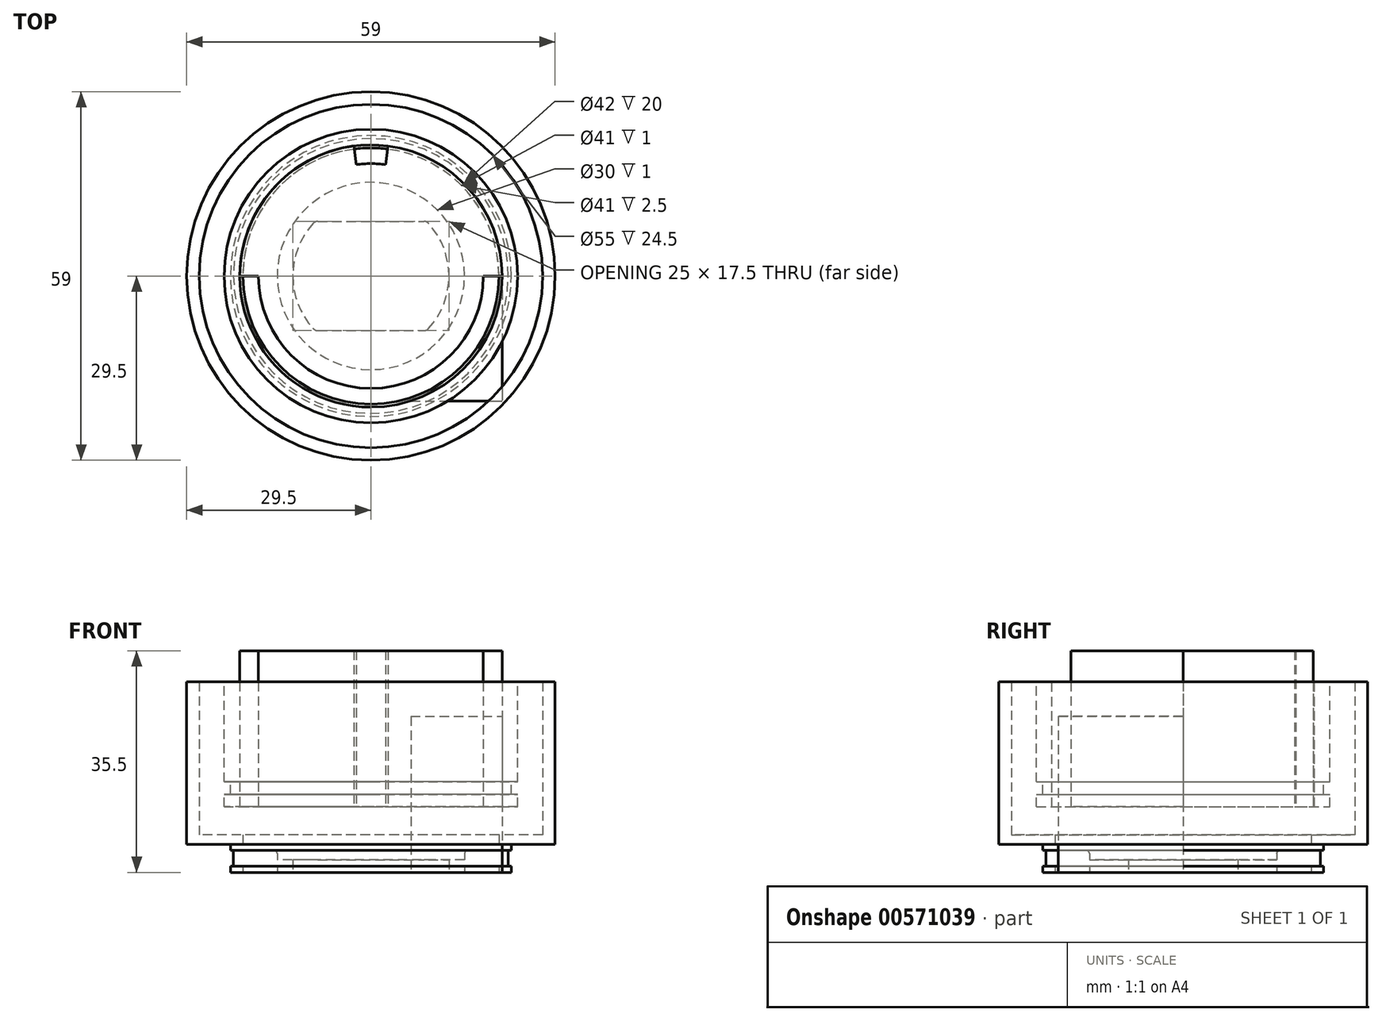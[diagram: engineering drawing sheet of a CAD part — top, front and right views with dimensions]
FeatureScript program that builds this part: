
annotation { "Feature Type Name" : "Feature", "Feature Type Description" : "" }
export const myFeature = defineFeature(function(context is Context, id is Id, definition is map)
    precondition{}
    {
        {
            var Q0;
            Q0=qCreatedBy(makeId("Top.planeOp"),FACE);
            var sketch = newSketch(context, id + "F0", { "sketchPlane" : qUnion([Q0])});
            skCircle(sketch, "E0", {"center": v(0, 0) * mm, "radius": 29.5 * mm});
            skCircle(sketch, "E1", {"center": v(0, 0) * mm, "radius": 22.5 * mm});
            skCircle(sketch, "E2", {"center": v(0, 0) * mm, "radius": 20.5 * mm});
            skCircle(sketch, "E3", {"center": v(0, 0) * mm, "radius": 15 * mm});
            skCircle(sketch, "E4", {"center": v(0, 0) * mm, "radius": 12.5 * mm, "construction": true});
            skLineSegment(sketch, "E5", {"start": v(-42, 8.75) * mm, "end": v(-42, -8.75) * mm, "construction": true});
            skPoint(sketch, "E6", {"position": v(-42, 0) * mm});
            skLineSegment(sketch, "E7", {"start": v(-8.5, 8.75) * mm, "end": v(8.5, 8.75) * mm});
            skLineSegment(sketch, "E8", {"start": v(-8.5, -8.75) * mm, "end": v(8.5, -8.75) * mm});
            skArc(sketch, "E9", {"start": v(-9.24, 8.42) * mm, "mid": v(-12.5, 0) * mm, "end": v(-9.24, -8.42) * mm});
            skArc(sketch, "E10", {"start": v(9.24, 8.42) * mm, "mid": v(12.5, 0) * mm, "end": v(9.24, -8.42) * mm});
            skPoint(sketch, "E11.visualSharp", {"position": v(-8.93, 8.75) * mm});
            skArc(sketch, "E11.filletArc", {"start": v(-8.5, 8.75) * mm, "mid": v(-8.9, 8.66) * mm, "end": v(-9.24, 8.42) * mm});
            skPoint(sketch, "E12.visualSharp", {"position": v(8.93, 8.75) * mm});
            skArc(sketch, "E12.filletArc", {"start": v(9.24, 8.42) * mm, "mid": v(8.9, 8.66) * mm, "end": v(8.5, 8.75) * mm});
            skPoint(sketch, "E13.visualSharp", {"position": v(-8.93, -8.75) * mm});
            skArc(sketch, "E13.filletArc", {"start": v(-9.24, -8.42) * mm, "mid": v(-8.9, -8.66) * mm, "end": v(-8.5, -8.75) * mm});
            skPoint(sketch, "E14.visualSharp", {"position": v(8.93, -8.75) * mm});
            skArc(sketch, "E14.filletArc", {"start": v(8.5, -8.75) * mm, "mid": v(8.9, -8.66) * mm, "end": v(9.24, -8.42) * mm});
            skCircle(sketch, "E15", {"center": v(0, 0) * mm, "radius": 22 * mm});
            skCircle(sketch, "E16", {"center": v(0, 0) * mm, "radius": 27.5 * mm});
            skSolve(sketch);
        }
        {
            var Q0;
            Q0=makeQuery(id+"F0.imprint","IMPRINT",FACE,{"disambiguationData":[TD([[makeQuery(id+"F0.imprint","IMPRINT",EDGE,{"derivedFrom":sQuery(id+"F0.wireOp",EDGE,"E1")}),1.0]])]});
            var Q1;
            Q1=makeQuery(id+"F0.imprint","IMPRINT",FACE,{"disambiguationData":[TD([[makeQuery(id+"F0.imprint","IMPRINT",EDGE,{"derivedFrom":sQuery(id+"F0.wireOp",EDGE,"E2")}),-1.0]])]});
            extrude(context, id + "F1", {"entities" : qUnion([Q0, Q1]), "depth" : 1 * mm, "offsetDistance" : 25 * mm});
        }
        {
            var Q0;
            Q0=makeQuery(id+"F0.imprint","IMPRINT",FACE,{"disambiguationData":[TD([[makeQuery(id+"F0.imprint","IMPRINT",EDGE,{"derivedFrom":sQuery(id+"F0.wireOp",EDGE,"E2")}),-1.0]])]});
            var Q1;
            Q1=makeQuery(id+"F0.imprint","IMPRINT",FACE,{"disambiguationData":[TD([[makeQuery(id+"F0.imprint","IMPRINT",EDGE,{"derivedFrom":sQuery(id+"F0.wireOp",EDGE,"E2")}),1.0]])]});
            extrude(context, id + "F2", {"entities" : qUnion([Q0, Q1]), "operationType" : NewBodyOperationType.ADD, "depth" : 3.5 * mm, "offsetDistance" : 25 * mm, "hasSecondDirection" : true, "secondDirectionOppositeDirection" : false, "secondDirectionDepth" : 1 * mm});
        }
        {
            var Q0;
            Q0=makeQuery(id+"F0.imprint","IMPRINT",FACE,{"disambiguationData":[TD([[makeQuery(id+"F0.imprint","IMPRINT",EDGE,{"derivedFrom":sQuery(id+"F0.wireOp",EDGE,"E1")}),1.0]])]});
            var Q1;
            Q1=makeQuery(id+"F0.imprint","IMPRINT",FACE,{"disambiguationData":[TD([[makeQuery(id+"F0.imprint","IMPRINT",EDGE,{"derivedFrom":sQuery(id+"F0.wireOp",EDGE,"E2")}),-1.0]])]});
            extrude(context, id + "F3", {"entities" : qUnion([Q0, Q1]), "operationType" : NewBodyOperationType.ADD, "depth" : 4.5 * mm, "offsetDistance" : 25 * mm, "hasSecondDirection" : true, "secondDirectionOppositeDirection" : false, "secondDirectionDepth" : 3.5 * mm});
        }
        {
            var Q0;
            Q0=makeQuery(id+"F0.imprint","IMPRINT",FACE,{"disambiguationData":[TD([[makeQuery(id+"F0.imprint","IMPRINT",EDGE,{"derivedFrom":sQuery(id+"F0.wireOp",EDGE,"E0")}),1.0]])]});
            var Q1;
            Q1=makeQuery(id+"F0.imprint","IMPRINT",FACE,{"disambiguationData":[TD([[makeQuery(id+"F0.imprint","IMPRINT",EDGE,{"derivedFrom":sQuery(id+"F0.wireOp",EDGE,"E2")}),-1.0]])]});
            var Q2;
            Q2=makeQuery(id+"F0.imprint","IMPRINT",FACE,{"disambiguationData":[TD([[makeQuery(id+"F0.imprint","IMPRINT",EDGE,{"derivedFrom":sQuery(id+"F0.wireOp",EDGE,"E1")}),1.0]])]});
            var Q3;
            Q3=makeQuery(id+"F0.imprint","IMPRINT",FACE,{"disambiguationData":[TD([[makeQuery(id+"F0.imprint","IMPRINT",EDGE,{"derivedFrom":sQuery(id+"F0.wireOp",EDGE,"E1")}),-1.0]])]});
            extrude(context, id + "F4", {"entities" : qUnion([Q0, Q1, Q2, Q3]), "operationType" : NewBodyOperationType.ADD, "depth" : 6 * mm, "offsetDistance" : 25 * mm, "hasSecondDirection" : true, "secondDirectionOppositeDirection" : false, "secondDirectionDepth" : 4.5 * mm});
        }
        {
            var Q0;
            Q0=makeQuery(id+"F0.imprint","IMPRINT",FACE,{"disambiguationData":[TD([[makeQuery(id+"F0.imprint","IMPRINT",EDGE,{"derivedFrom":sQuery(id+"F0.wireOp",EDGE,"E3")}),1.0]])]});
            extrude(context, id + "F5", {"entities" : qUnion([Q0]), "operationType" : NewBodyOperationType.ADD, "depth" : 2 * mm, "offsetDistance" : 25 * mm});
        }
        {
            var Q0;
            Q0=makeQuery(id+"F0.imprint","IMPRINT",FACE,{"disambiguationData":[TD([[makeQuery(id+"F0.imprint","IMPRINT",EDGE,{"derivedFrom":sQuery(id+"F0.wireOp",EDGE,"E0")}),1.0]])]});
            extrude(context, id + "F6", {"entities" : qUnion([Q0]), "operationType" : NewBodyOperationType.ADD, "depth" : (44 - 18 + 4.5) * mm, "offsetDistance" : 25 * mm, "hasSecondDirection" : true, "secondDirectionOppositeDirection" : false, "secondDirectionDepth" : 6 * mm});
        }
        {
            var Q0;
            Q0=makeQuery(id+"F2.opExtrude","CAP_EDGE",EDGE,{"disambiguationData":[OSD([sQuery(id+"F0.wireOp",EDGE,"E3")])],"isStart":false});
            fillet(context, id + "F7", {"entities" : qUnion([Q0]), "radius" : 0.5 * mm, "tangentPropagation" : true, "allowEdgeOverflow" : false});
        }
        {
            var Q0;
            Q0=qCreatedBy(makeId("Top.planeOp"),FACE);
            var sketch = newSketch(context, id + "F8", { "sketchPlane" : qUnion([Q0])});
            skCircle(sketch, "E17", {"center": v(0, 0) * mm, "radius": 23.5 * mm, "construction": true});
            skLineSegment(sketch, "E18.bottom", {"start": v(-23.5, 0) * mm, "end": v(23.5, 0) * mm});
            skLineSegment(sketch, "E18.top", {"start": v(-23.5, -20) * mm, "end": v(23.5, -20) * mm});
            skLineSegment(sketch, "E18.left", {"start": v(-23.5, 0) * mm, "end": v(-23.5, -2) * mm});
            skLineSegment(sketch, "E18.right", {"start": v(23.5, 0) * mm, "end": v(23.5, -2) * mm});
            skCircle(sketch, "E19", {"center": v(0, 0) * mm, "radius": 21 * mm});
            skLineSegment(sketch, "E20", {"start": v(22.5, -2) * mm, "end": v(22.5, -4) * mm});
            skPoint(sketch, "E21", {"position": v(21, 0) * mm});
            skPoint(sketch, "E22", {"position": v(-21, 0) * mm});
            skCircle(sketch, "E23", {"center": v(0, 0) * mm, "radius": 22.5 * mm, "construction": true});
            skLineSegment(sketch, "E24", {"start": v(21, 0) * mm, "end": v(21, -20) * mm});
            skLineSegment(sketch, "E25", {"start": v(-21, 0) * mm, "end": v(-21, -20) * mm});
            skLineSegment(sketch, "E26", {"start": v(23.5, -2) * mm, "end": v(22.5, -2) * mm});
            skLineSegment(sketch, "E27", {"start": v(22.5, -4) * mm, "end": v(23.5, -4) * mm});
            skLineSegment(sketch, "E28.trimOffspring", {"start": v(23.5, -4) * mm, "end": v(23.5, -20) * mm});
            skPoint(sketch, "E29", {"position": v(-22.5, 0) * mm});
            skLineSegment(sketch, "E30", {"start": v(-23.5, -2) * mm, "end": v(-22.5, -2) * mm});
            skLineSegment(sketch, "E31", {"start": v(-22.5, -2) * mm, "end": v(-22.5, -4) * mm});
            skLineSegment(sketch, "E32", {"start": v(-22.5, -4) * mm, "end": v(-23.5, -4) * mm});
            skLineSegment(sketch, "E33", {"start": v(-23.5, -4) * mm, "end": v(-23.5, -20) * mm});
            skLineSegment(sketch, "E34", {"start": v(0, -49.3) * mm, "end": v(0, 33.34) * mm, "construction": true});
            skPoint(sketch, "E34.startSnap0", {"position": v(0, -20) * mm});
            skCircle(sketch, "E35", {"center": v(0, 0) * mm, "radius": 18 * mm});
            skLineSegment(sketch, "E36", {"start": v(0, 0) * mm, "end": v(-3.77, 28.6) * mm});
            skLineSegment(sketch, "E37", {"start": v(0, 0) * mm, "end": v(3.77, 28.6) * mm});
            skSolve(sketch);
        }
        {
            var Q0;
            {var subQ0=sQuery(id+"F8.wireOp",EDGE,"E18.left");Q0=makeQuery(id+"F8.imprint","IMPRINT",FACE,{"disambiguationData":[TD([[makeQuery(id+"F8.imprint","IMPRINT",EDGE,{"derivedFrom":subQ0}),1.0]])]});}
            var Q1;
            Q1=sQuery(id+"F8.wireOp",EDGE,"E34");
            revolve(context, id + "F9", {"entities" : qUnion([Q0]), "axis" : qUnion([Q1]), "revolveType" : RevolveType.FULL});
        }
        {
            var Q0;
            {var subQ1=sQuery(id+"F8.wireOp",EDGE,"E18.bottom");var subQ3=sQuery(id+"F8.wireOp",EDGE,"E35");var subQ4=makeQuery(id+"F8.imprint","INTERSECT",VERTEX,{"disambiguationData":[OD(0.0)],"derivedFrom":[subQ1,subQ3]});Q0=makeQuery(id+"F8.imprint","IMPRINT",FACE,{"disambiguationData":[TD([[makeQuery(id+"F8.imprint","IMPRINT",EDGE,{"disambiguationData":[TD([[subQ4,1.0]])],"derivedFrom":subQ3}),-1.0]])]});}
            var Q1;
            {var subQ1=sQuery(id+"F8.wireOp",EDGE,"E18.bottom");var subQ3=sQuery(id+"F8.wireOp",EDGE,"E35");var subQ4=makeQuery(id+"F8.imprint","INTERSECT",VERTEX,{"disambiguationData":[OD(0.0)],"derivedFrom":[subQ1,subQ3]});Q1=makeQuery(id+"F8.imprint","IMPRINT",FACE,{"disambiguationData":[TD([[makeQuery(id+"F8.imprint","IMPRINT",EDGE,{"disambiguationData":[TD([[subQ4,1.0]])],"derivedFrom":subQ3}),1.0]])]});}
            var Q2;
            {var subQ1=sQuery(id+"F8.wireOp",EDGE,"E18.bottom");var subQ3=sQuery(id+"F8.wireOp",EDGE,"E35");var subQ4=makeQuery(id+"F8.imprint","INTERSECT",VERTEX,{"disambiguationData":[OD(1.0)],"derivedFrom":[subQ1,subQ3]});Q2=makeQuery(id+"F8.imprint","IMPRINT",FACE,{"disambiguationData":[TD([[makeQuery(id+"F8.imprint","IMPRINT",EDGE,{"disambiguationData":[TD([[subQ4,-1.0]])],"derivedFrom":subQ3}),1.0]])]});}
            var Q3;
            {var subQ1=sQuery(id+"F8.wireOp",EDGE,"E18.bottom");var subQ3=sQuery(id+"F8.wireOp",EDGE,"E35");var subQ4=makeQuery(id+"F8.imprint","INTERSECT",VERTEX,{"disambiguationData":[OD(1.0)],"derivedFrom":[subQ1,subQ3]});Q3=makeQuery(id+"F8.imprint","IMPRINT",FACE,{"disambiguationData":[TD([[makeQuery(id+"F8.imprint","IMPRINT",EDGE,{"disambiguationData":[TD([[subQ4,-1.0]])],"derivedFrom":subQ3}),-1.0]])]});}
            var Q4;
            {var subQ0=sQuery(id+"F8.wireOp",EDGE,"E37");var subQ1=sQuery(id+"F8.wireOp",EDGE,"E35");var subQ2=makeQuery(id+"F8.imprint","INTERSECT",VERTEX,{"derivedFrom":[subQ1,subQ0]});Q4=makeQuery(id+"F8.imprint","IMPRINT",FACE,{"disambiguationData":[TD([[makeQuery(id+"F8.imprint","IMPRINT",EDGE,{"disambiguationData":[TD([[subQ2,-1.0]])],"derivedFrom":subQ1}),1.0]])]});}
            var Q5;
            {var subQ0=sQuery(id+"F8.wireOp",EDGE,"E18.bottom");var subQ2=sQuery(id+"F8.wireOp",EDGE,"E35");var subQ3=makeQuery(id+"F8.imprint","INTERSECT",VERTEX,{"disambiguationData":[OD(0.0)],"derivedFrom":[subQ0,subQ2]});Q5=makeQuery(id+"F8.imprint","IMPRINT",FACE,{"disambiguationData":[TD([[makeQuery(id+"F8.imprint","IMPRINT",EDGE,{"disambiguationData":[TD([[subQ3,-1.0]])],"derivedFrom":subQ2}),1.0]])]});}
            var Q6;
            {var subQ0=sQuery(id+"F8.wireOp",EDGE,"E19");var subQ1=sQuery(id+"F8.wireOp",EDGE,"E18.top");var subQ2=makeQuery(id+"F8.imprint","INTERSECT",VERTEX,{"disambiguationData":[OD(0.0)],"derivedFrom":[subQ1,subQ0]});Q6=makeQuery(id+"F8.imprint","IMPRINT",FACE,{"disambiguationData":[TD([[makeQuery(id+"F8.imprint","IMPRINT",EDGE,{"disambiguationData":[TD([[subQ2,-1.0]])],"derivedFrom":subQ1}),1.0]])]});}
            var Q7;
            {var subQ0=sQuery(id+"F8.wireOp",EDGE,"E19");var subQ1=sQuery(id+"F8.wireOp",EDGE,"E18.top");var subQ2=makeQuery(id+"F8.imprint","INTERSECT",VERTEX,{"disambiguationData":[OD(0.0)],"derivedFrom":[subQ1,subQ0]});Q7=makeQuery(id+"F8.imprint","IMPRINT",FACE,{"disambiguationData":[TD([[makeQuery(id+"F8.imprint","IMPRINT",EDGE,{"disambiguationData":[TD([[subQ2,-1.0]])],"derivedFrom":subQ1}),-1.0]])]});}
            extrude(context, id + "F10", {"entities" : qUnion([Q0, Q1, Q2, Q3, Q4, Q5, Q6, Q7]), "depth" : 25 * mm, "offsetDistance" : 25 * mm});
        }
        {
            var Q0;
            Q0=makeQuery(id+"F9.opRevolve","SWEPT_BODY",BODY,{"disambiguationData":[OSD([sQuery(id+"F8.wireOp",EDGE,"E18.bottom"),sQuery(id+"F8.wireOp",EDGE,"E18.top"),sQuery(id+"F8.wireOp",EDGE,"E18.left"),sQuery(id+"F8.wireOp",EDGE,"E25"),sQuery(id+"F8.wireOp",EDGE,"E30"),sQuery(id+"F8.wireOp",EDGE,"E31"),sQuery(id+"F8.wireOp",EDGE,"E32"),sQuery(id+"F8.wireOp",EDGE,"E33")])]});
            var Q1;
            Q1=sQuery(id+"F8.wireOp",EDGE,"E18.bottom");
            transform(context, id + "F11", {"entities" : qUnion([Q0]), "transformType" : TransformType.ROTATION, "transformAxis" : qUnion([Q1]), "angle" : 90 * degree, "oppositeDirection" : true, "makeCopy" : false});
        }
        {
            var Q0;
            Q0=makeQuery(id+"F9.opRevolve","SWEPT_BODY",BODY,{"disambiguationData":[OSD([sQuery(id+"F8.wireOp",EDGE,"E18.bottom"),sQuery(id+"F8.wireOp",EDGE,"E18.top"),sQuery(id+"F8.wireOp",EDGE,"E18.left"),sQuery(id+"F8.wireOp",EDGE,"E25"),sQuery(id+"F8.wireOp",EDGE,"E30"),sQuery(id+"F8.wireOp",EDGE,"E31"),sQuery(id+"F8.wireOp",EDGE,"E32"),sQuery(id+"F8.wireOp",EDGE,"E33")])]});
            var Q1;
            Q1=makeQuery(id+"F10.opExtrude","SWEPT_BODY",BODY,{"disambiguationData":[OSD([sQuery(id+"F8.wireOp",EDGE,"E19"),sQuery(id+"F8.wireOp",EDGE,"E35"),sQuery(id+"F8.wireOp",EDGE,"E36"),sQuery(id+"F8.wireOp",EDGE,"E37")])]});
            transform(context, id + "F12", {"entities" : qUnion([Q0, Q1]), "transformType" : TransformType.TRANSLATION_3D, "dx" : 0 * mm, "dy" : 0 * mm, "dz" : (4.5 + 6) * mm, "makeCopy" : false});
        }
    });
